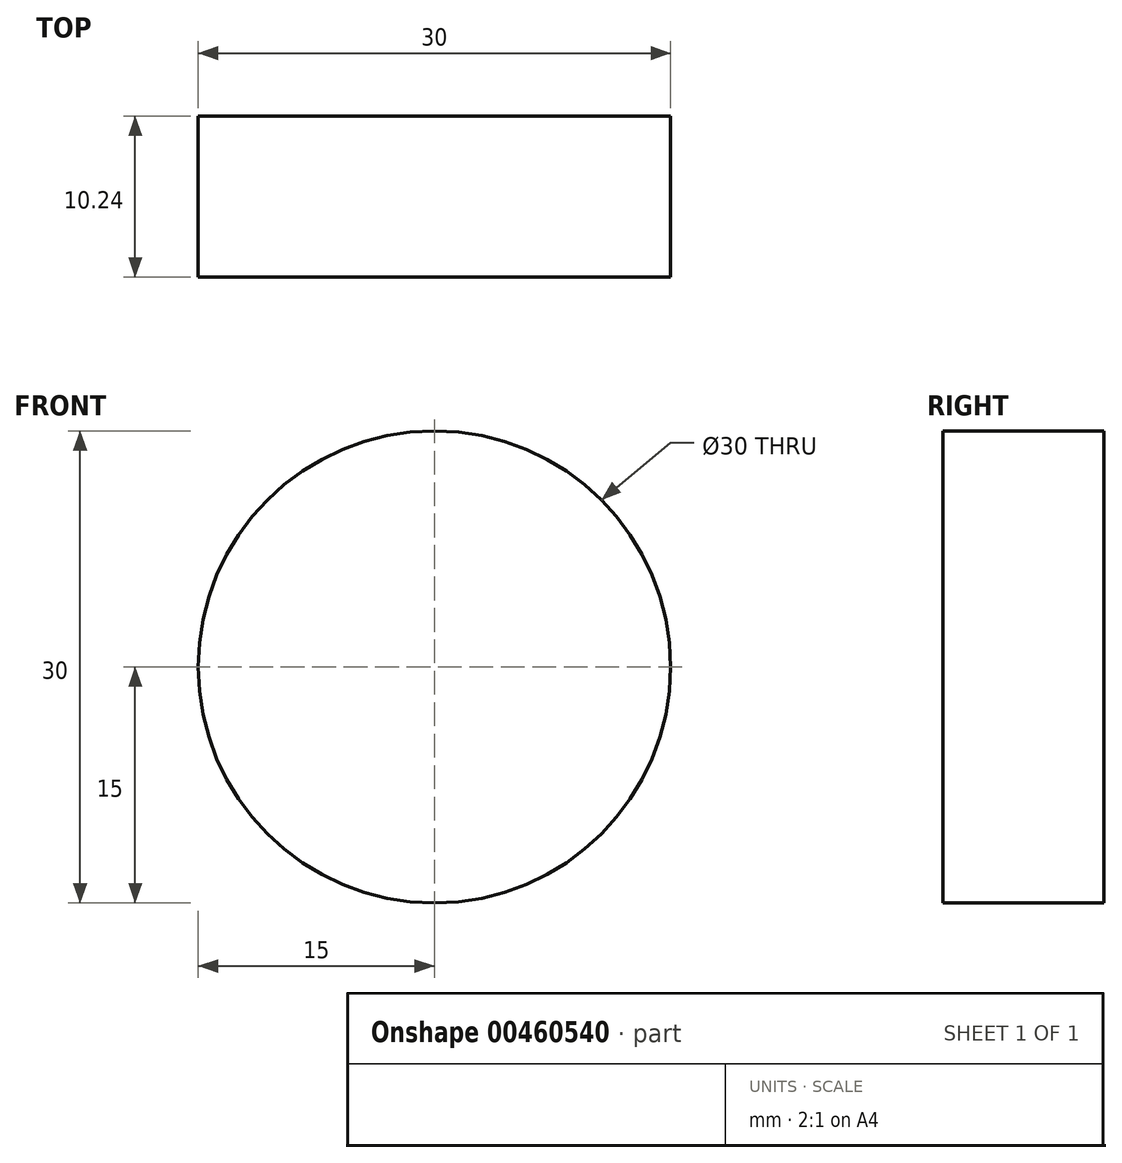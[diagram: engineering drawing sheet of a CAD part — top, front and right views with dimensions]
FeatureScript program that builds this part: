
annotation { "Feature Type Name" : "Feature", "Feature Type Description" : "" }
export const myFeature = defineFeature(function(context is Context, id is Id, definition is map)
    precondition{}
    {
        {
            var Q0;
            Q0=qCreatedBy(makeId("Front.planeOp"),FACE);
            var sketch = newSketch(context, id + "F0", { "sketchPlane" : qUnion([Q0])});
            skCircle(sketch, "E0", {"center": v(0, 0) * mm, "radius": 15 * mm});
            skSolve(sketch);
        }
        {
            var Q0;
            Q0 = qBodyType(qCreatedBy(id + "F0" ,EDGE), BodyType.WIRE);
            extrude(context, id + "F1", {"bodyType" : ToolBodyType.SURFACE, "surfaceEntities" : qUnion([Q0]), "oppositeDirection" : true, "depth" : 10.24 * mm});
        }
    });
